# Revit family: LP110 Mist
name_source: partatom
category: Lighting Fixtures
units: mm (PartAtom-declared; Revit-internal decimal feet)

## family parameters
Always vertical = Yes
Cut with Voids When Loaded = No
Host = Ceiling
Light Source = Yes
OmniClass Number = 23.80.70.11
OmniClass Title = Luminaries for Internal Lighting
Part Type = Normal
Room Calculation Point = No
Round Connector Dimension = Use Diameter
Shared = No

## types (2) — shared parameters
ABOVE CEILING MATERIAL = <By Category>
AssetType = Fixed
BaseHeight = 26mm Exposed Surface / 55mm Internal from install surface
Central Material = Central Material
CodePerformance = IEC60598-1 / EN1365-2:2014 /BS 8458: 2015
Color = White - RAL 9016
Color Filter = 16777215
Dimming Lamp Color Temperature Shift = <None>
DurationUnit = Year
ElectricalDeviceNominalPower = 8.2W
Emit Shape Visible in Rendering = No
Emit from Circle Diameter = 610 mm
ExpectedLife = 5 Years / 50,000Hrs
Finish = Satin
General Material = General Material
Grill Material = Grill Material
HasProtectiveEarth = False
Humidity = 0-85% RH
IP_Code = IP65
Inner Ring Material = Inner Ring Material
InsulationStandardClass = IC-4
Light Material = Default Light Source
ManufacturerName = Lumi-Plugin Ltd
Material = Polycarbonate UL94-V0 / Stainless Steel 430 / Polypropylene UL94-V0
NBSDescription = LP110 Downlight with Mist Suppression
Name = Lumi-Mist
NominalHeight = 26mm Exposed Surface / 55mm Internal from install surface
NominalLength = 110mm
NominalVoltage = 220V-240V AC 50Hz
Outer Ring = 166_72_0
ProductInformation = https://www.lumi-plugin.com
Shape = Circular
Size = 110mm DIA / 26mm Exposed Surface / 55mm Internal from install surface
Tilt Angle = 90.00°
Uniclass2015Code = Pr_70_55_98_84
Uniclass2015Title = Sprinklers
UsageCurrent = 50Hz 0.050A
WarrantyDescription = Check date code on product label for date of manufacture
WarrantyDurationLabor = 5yr
WarrantyDurationParts = 5yr
WarrantyDurationUnit = Year
WarrantyGuarantorLabor = https://www.lumi-plugin.com
WarrantyGuarantorParts = https://www.lumi-plugin.com
WarrantyStartDate = At date of purchase
Weight = 466g
zero-valued in all types: Default Elevation

## per-type parameters (varying)
| type | BIMObjectName | Features | ModelNumber | Photometric Web File |
| 4000K | Lumi-Mist (LP110WH4KIMIST) | 600lm, 100deg Beam Angle, IP65, 30/60/90 Fire Rated 4000K Downlight with intergrated IMIST Water Mist Fire Suppression | LP110WH4KIMIST | LP110 DVT 4000K HOT 20191210_IESNA95.IES |
| 3000K | Lumi-Mist (LP110WH3KIMIST) | 600lm, 100deg Beam Angle, IP65, 30/60/90 Fire Rated 3000K Downlight with intergrated IMIST Water Mist Fire Suppression | LP110WH3KIMIST | LP110 DVT 3000K HOT 20191210_IESNA95.IES |

## geometry (parser evidence)
native form markers: Sweep x2
no freeform markers — native parametric forms only
